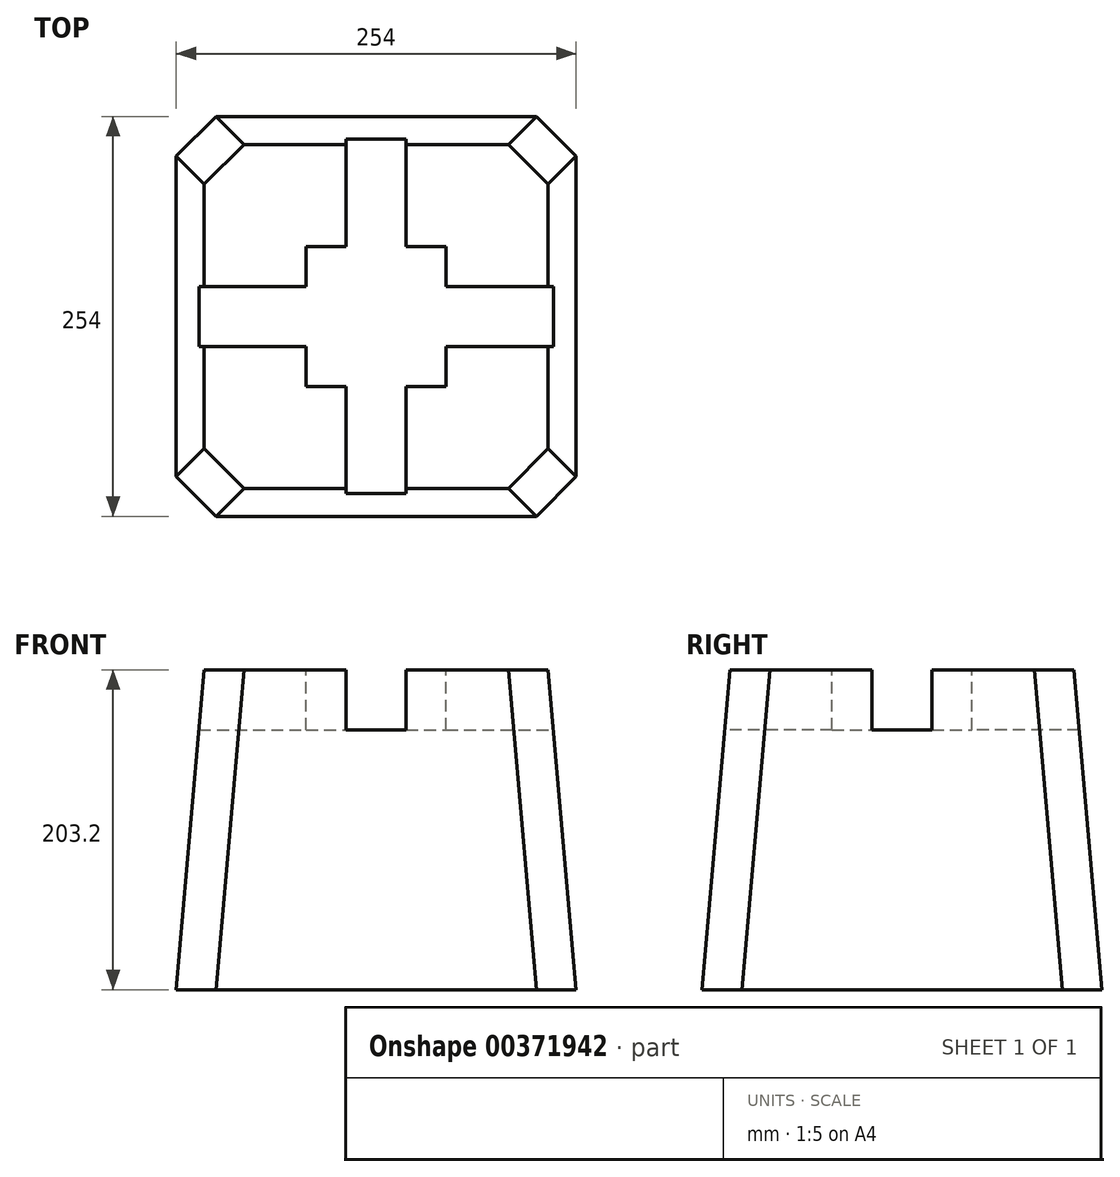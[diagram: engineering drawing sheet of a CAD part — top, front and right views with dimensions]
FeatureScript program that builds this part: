
annotation { "Feature Type Name" : "Feature", "Feature Type Description" : "" }
export const myFeature = defineFeature(function(context is Context, id is Id, definition is map)
    precondition{}
    {
        {
            var Q0;
            Q0=qCreatedBy(makeId("Top.planeOp"),FACE);
            var sketch = newSketch(context, id + "F0", { "sketchPlane" : qUnion([Q0])});
            skLineSegment(sketch, "E0.bottom", {"start": v(-127, -127) * mm, "end": v(127, -127) * mm});
            skLineSegment(sketch, "E0.top", {"start": v(-127, 127) * mm, "end": v(127, 127) * mm});
            skLineSegment(sketch, "E0.left", {"start": v(-127, -127) * mm, "end": v(-127, 127) * mm});
            skLineSegment(sketch, "E0.right", {"start": v(127, -127) * mm, "end": v(127, 127) * mm});
            skSolve(sketch);
        }
        {
            var Q0;
            Q0=qSketchRegion(id+"F0",true);
            extrude(context, id + "F1", {"entities" : qUnion([Q0]), "depth" : 203.2 * mm, "hasDraft" : true, "draftAngle" : 5 * degree, "draftPullDirection" : true});
        }
        {
            var Q0;
            Q0=makeQuery(id+"F1.opExtrude","SWEPT_EDGE",EDGE,{"disambiguationData":[OSD([sQuery(id+"F0.wireOp",EDGE,"E0.bottom"),sQuery(id+"F0.wireOp",EDGE,"E0.left")])]});
            var Q1;
            Q1=makeQuery(id+"F1.opExtrude","SWEPT_EDGE",EDGE,{"disambiguationData":[OSD([sQuery(id+"F0.wireOp",EDGE,"E0.bottom"),sQuery(id+"F0.wireOp",EDGE,"E0.right")])]});
            var Q2;
            Q2=makeQuery(id+"F1.opExtrude","SWEPT_EDGE",EDGE,{"disambiguationData":[OSD([sQuery(id+"F0.wireOp",EDGE,"E0.top"),sQuery(id+"F0.wireOp",EDGE,"E0.right")])]});
            var Q3;
            Q3=makeQuery(id+"F1.opExtrude","SWEPT_EDGE",EDGE,{"disambiguationData":[OSD([sQuery(id+"F0.wireOp",EDGE,"E0.top"),sQuery(id+"F0.wireOp",EDGE,"E0.left")])]});
            chamfer(context, id + "F2", {"entities" : qUnion([Q0, Q1, Q2, Q3]), "width" : 25.4 * mm, "tangentPropagation" : true});
        }
        {
            var Q0;
            Q0=makeQuery(id+"F1.opExtrude","CAP_FACE",FACE,{"disambiguationData":[OSD([sQuery(id+"F0.wireOp",EDGE,"E0.bottom"),sQuery(id+"F0.wireOp",EDGE,"E0.top"),sQuery(id+"F0.wireOp",EDGE,"E0.left"),sQuery(id+"F0.wireOp",EDGE,"E0.right")])],"isStart":false});
            var sketch = newSketch(context, id + "F3", { "sketchPlane" : qUnion([Q0])});
            skLineSegment(sketch, "E1", {"start": v(0, 109.22) * mm, "end": v(0, -109.22) * mm, "construction": true});
            skLineSegment(sketch, "E2", {"start": v(-109.22, 0) * mm, "end": v(109.22, 0) * mm, "construction": true});
            skLineSegment(sketch, "E3.0", {"start": v(19.05, 132.02) * mm, "end": v(19.05, 44.45) * mm});
            skLineSegment(sketch, "E4.0", {"start": v(-19.05, 132.02) * mm, "end": v(-19.05, 44.45) * mm});
            skLineSegment(sketch, "E5.0", {"start": v(-137.83, -19.05) * mm, "end": v(-44.45, -19.05) * mm});
            skLineSegment(sketch, "E6.0", {"start": v(-137.83, 19.05) * mm, "end": v(-44.45, 19.05) * mm});
            skLineSegment(sketch, "E7.trimOffspring", {"start": v(-19.05, -44.45) * mm, "end": v(-19.05, -130.36) * mm});
            skLineSegment(sketch, "E8.trimOffspring", {"start": v(44.45, 19.05) * mm, "end": v(136.5, 19.05) * mm});
            skLineSegment(sketch, "E9.trimOffspring", {"start": v(19.05, -44.45) * mm, "end": v(19.05, -130.36) * mm});
            skLineSegment(sketch, "E10.trimOffspring", {"start": v(44.45, -19.05) * mm, "end": v(136.5, -19.05) * mm});
            skLineSegment(sketch, "E11.bottom", {"start": v(-44.45, -44.45) * mm, "end": v(-19.05, -44.45) * mm});
            skLineSegment(sketch, "E11.top", {"start": v(-44.45, 44.45) * mm, "end": v(-19.05, 44.45) * mm});
            skLineSegment(sketch, "E11.left", {"start": v(-44.45, -44.45) * mm, "end": v(-44.45, -19.05) * mm});
            skLineSegment(sketch, "E11.right", {"start": v(44.45, -44.45) * mm, "end": v(44.45, -19.05) * mm});
            skLineSegment(sketch, "E12.trimOffspring", {"start": v(19.05, 44.45) * mm, "end": v(44.45, 44.45) * mm});
            skLineSegment(sketch, "E13.trimOffspring", {"start": v(44.45, 19.05) * mm, "end": v(44.45, 44.45) * mm});
            skLineSegment(sketch, "E14.trimOffspring", {"start": v(19.05, -44.45) * mm, "end": v(44.45, -44.45) * mm});
            skLineSegment(sketch, "E15.trimOffspring", {"start": v(-44.45, 19.05) * mm, "end": v(-44.45, 44.45) * mm});
            skLineSegment(sketch, "E16", {"start": v(-19.05, -130.36) * mm, "end": v(19.05, -130.36) * mm});
            skLineSegment(sketch, "E17", {"start": v(-137.83, -19.05) * mm, "end": v(-137.83, 19.05) * mm});
            skLineSegment(sketch, "E18", {"start": v(-19.05, 132.02) * mm, "end": v(19.05, 132.02) * mm});
            skLineSegment(sketch, "E19", {"start": v(136.5, 19.05) * mm, "end": v(136.5, -19.05) * mm});
            skPoint(sketch, "E20.orphan", {"position": v(-19.05, 104.78) * mm});
            skPoint(sketch, "E21.orphan", {"position": v(19.05, 104.78) * mm});
            skPoint(sketch, "E22.orphan", {"position": v(104.78, 19.05) * mm});
            skPoint(sketch, "E23.orphan", {"position": v(19.05, -104.78) * mm});
            skPoint(sketch, "E24.orphan", {"position": v(-19.05, -104.78) * mm});
            skPoint(sketch, "E25.orphan", {"position": v(-104.78, -19.05) * mm});
            skPoint(sketch, "E26.orphan", {"position": v(-104.78, 19.05) * mm});
            skSolve(sketch);
        }
        {
            var Q0;
            Q0=qSketchRegion(id+"F3",true);
            extrude(context, id + "F4", {"entities" : qUnion([Q0]), "operationType" : NewBodyOperationType.REMOVE, "oppositeDirection" : true, "depth" : 38.1 * mm});
        }
    });
